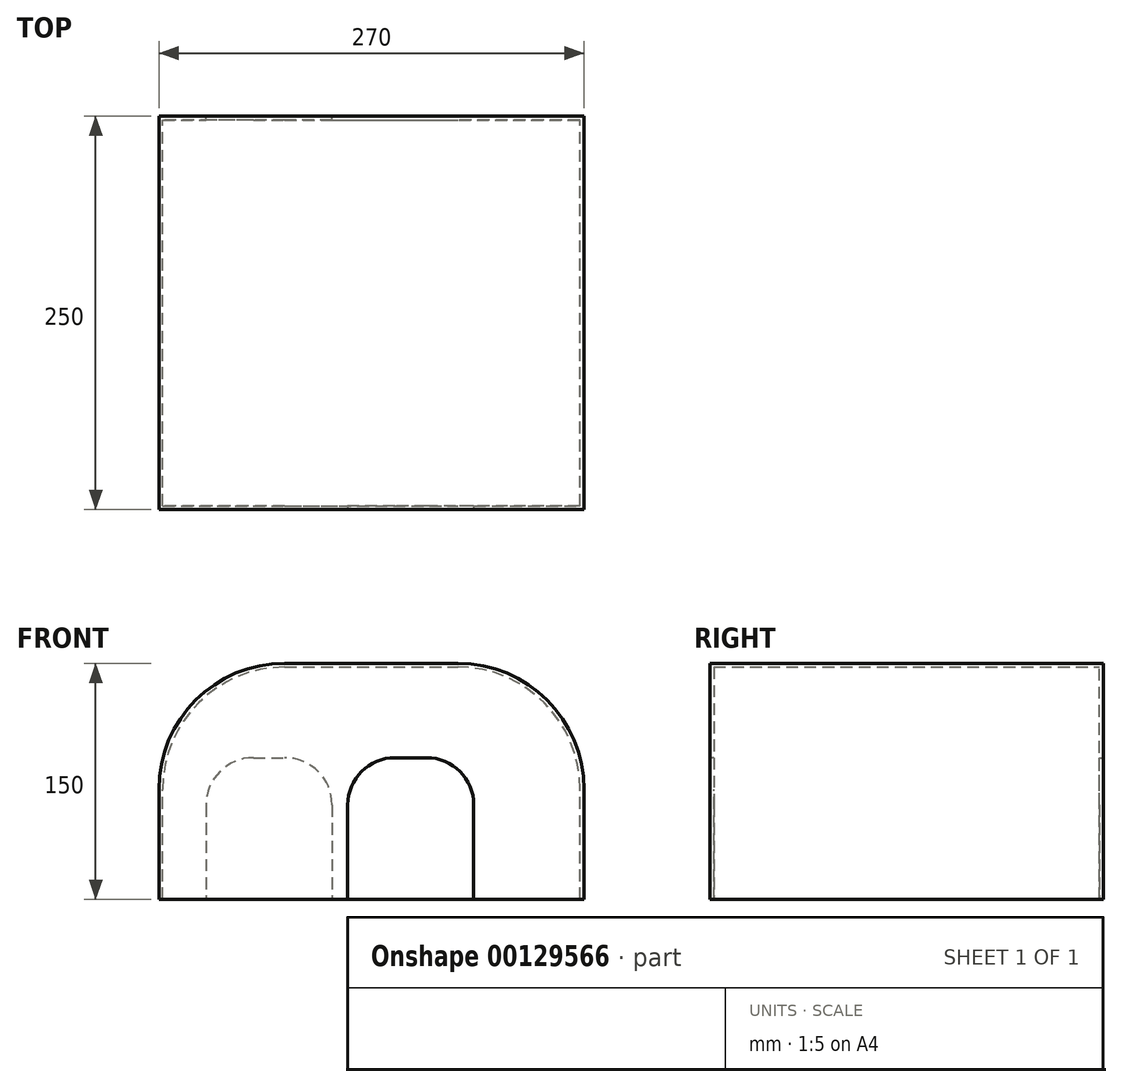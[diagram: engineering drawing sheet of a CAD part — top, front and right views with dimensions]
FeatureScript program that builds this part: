
annotation { "Feature Type Name" : "Feature", "Feature Type Description" : "" }
export const myFeature = defineFeature(function(context is Context, id is Id, definition is map)
    precondition{}
    {
        {
            var Q0;
            Q0=qCreatedBy(makeId("Front.planeOp"),FACE);
            var sketch = newSketch(context, id + "F0", { "sketchPlane" : qUnion([Q0])});
            skLineSegment(sketch, "E0.bottom", {"start": v(-135, 0) * mm, "end": v(135, 0) * mm});
            skLineSegment(sketch, "E0.top", {"start": v(-135, 150) * mm, "end": v(135, 150) * mm});
            skLineSegment(sketch, "E0.left", {"start": v(-135, 0) * mm, "end": v(-135, 150) * mm});
            skLineSegment(sketch, "E0.right", {"start": v(135, 0) * mm, "end": v(135, 150) * mm});
            skSolve(sketch);
        }
        {
            var Q0;
            Q0 = qSketchRegion(id + "F0", true);
            extrude(context, id + "F1", {"entities" : qUnion([Q0]), "depth" : 250 * mm});
        }
        {
            var Q0;
            Q0=makeQuery(id+"F1.opExtrude","SWEPT_EDGE",EDGE,{"disambiguationData":[OSD([sQuery(id+"F0.wireOp",EDGE,"E0.top"),sQuery(id+"F0.wireOp",EDGE,"E0.left")])]});
            var Q1;
            Q1=makeQuery(id+"F1.opExtrude","SWEPT_EDGE",EDGE,{"disambiguationData":[OSD([sQuery(id+"F0.wireOp",EDGE,"E0.top"),sQuery(id+"F0.wireOp",EDGE,"E0.right")])]});
            fillet(context, id + "F2", {"entities" : qUnion([Q0, Q1]), "radius" : 80 * mm, "tangentPropagation" : true, "allowEdgeOverflow" : false});
        }
        {
            var Q0;
            Q0=makeQuery(id+"F1.opExtrude","SWEPT_FACE",FACE,{"disambiguationData":[OSD([sQuery(id+"F0.wireOp",EDGE,"E0.bottom")])]});
            shell(context, id + "F3", {"entities" : qUnion([Q0]), "thickness" : 2.5 * mm});
        }
        {
            var Q0;
            Q0=makeQuery(id+"F1.opExtrude","CAP_FACE",FACE,{"disambiguationData":[OSD([sQuery(id+"F0.wireOp",EDGE,"E0.bottom"),sQuery(id+"F0.wireOp",EDGE,"E0.top"),sQuery(id+"F0.wireOp",EDGE,"E0.left"),sQuery(id+"F0.wireOp",EDGE,"E0.right")])],"isStart":false});
            var sketch = newSketch(context, id + "F4", { "sketchPlane" : qUnion([Q0])});
            skLineSegment(sketch, "E1.bottom", {"start": v(-15, 0) * mm, "end": v(65, 0) * mm});
            skLineSegment(sketch, "E1.top", {"start": v(15, 90) * mm, "end": v(35, 90) * mm});
            skLineSegment(sketch, "E1.left", {"start": v(-15, 0) * mm, "end": v(-15, 60) * mm});
            skLineSegment(sketch, "E1.right", {"start": v(65, 0) * mm, "end": v(65, 60) * mm});
            skPoint(sketch, "E2.visualSharp", {"position": v(-15, 90) * mm});
            skArc(sketch, "E2.filletArc", {"start": v(15, 90) * mm, "mid": v(-6.21, 81.21) * mm, "end": v(-15, 60) * mm});
            skPoint(sketch, "E3.visualSharp", {"position": v(65, 90) * mm});
            skArc(sketch, "E3.filletArc", {"start": v(65, 60) * mm, "mid": v(56.21, 81.21) * mm, "end": v(35, 90) * mm});
            skSolve(sketch);
        }
        {
            var Q0;
            Q0 = qSketchRegion(id + "F4", true);
            extrude(context, id + "F5", {"entities" : qUnion([Q0]), "operationType" : NewBodyOperationType.REMOVE, "endBound" : BoundingType.UP_TO_NEXT, "oppositeDirection" : true, "depth" : 25 * mm});
        }
        {
            var Q0;
            Q0=makeQuery(id+"F1.opExtrude","CAP_FACE",FACE,{"disambiguationData":[OSD([sQuery(id+"F0.wireOp",EDGE,"E0.bottom"),sQuery(id+"F0.wireOp",EDGE,"E0.top"),sQuery(id+"F0.wireOp",EDGE,"E0.left"),sQuery(id+"F0.wireOp",EDGE,"E0.right")])],"isStart":true});
            var sketch = newSketch(context, id + "F6", { "sketchPlane" : qUnion([Q0])});
            skLineSegment(sketch, "E4.bottom", {"start": v(25, 0) * mm, "end": v(105, 0) * mm});
            skLineSegment(sketch, "E4.top", {"start": v(55, 90) * mm, "end": v(75, 90) * mm});
            skLineSegment(sketch, "E4.left", {"start": v(25, 0) * mm, "end": v(25, 60) * mm});
            skLineSegment(sketch, "E4.right", {"start": v(105, 0) * mm, "end": v(105, 60) * mm});
            skPoint(sketch, "E5.visualSharp", {"position": v(25, 90) * mm});
            skArc(sketch, "E5.filletArc", {"start": v(55, 90) * mm, "mid": v(33.79, 81.21) * mm, "end": v(25, 60) * mm});
            skPoint(sketch, "E6.visualSharp", {"position": v(105, 90) * mm});
            skArc(sketch, "E6.filletArc", {"start": v(105, 60) * mm, "mid": v(96.21, 81.21) * mm, "end": v(75, 90) * mm});
            skSolve(sketch);
        }
        {
            var Q0;
            Q0 = qSketchRegion(id + "F6", true);
            extrude(context, id + "F7", {"entities" : qUnion([Q0]), "operationType" : NewBodyOperationType.REMOVE, "oppositeDirection" : true, "depth" : 25 * mm});
        }
    });
